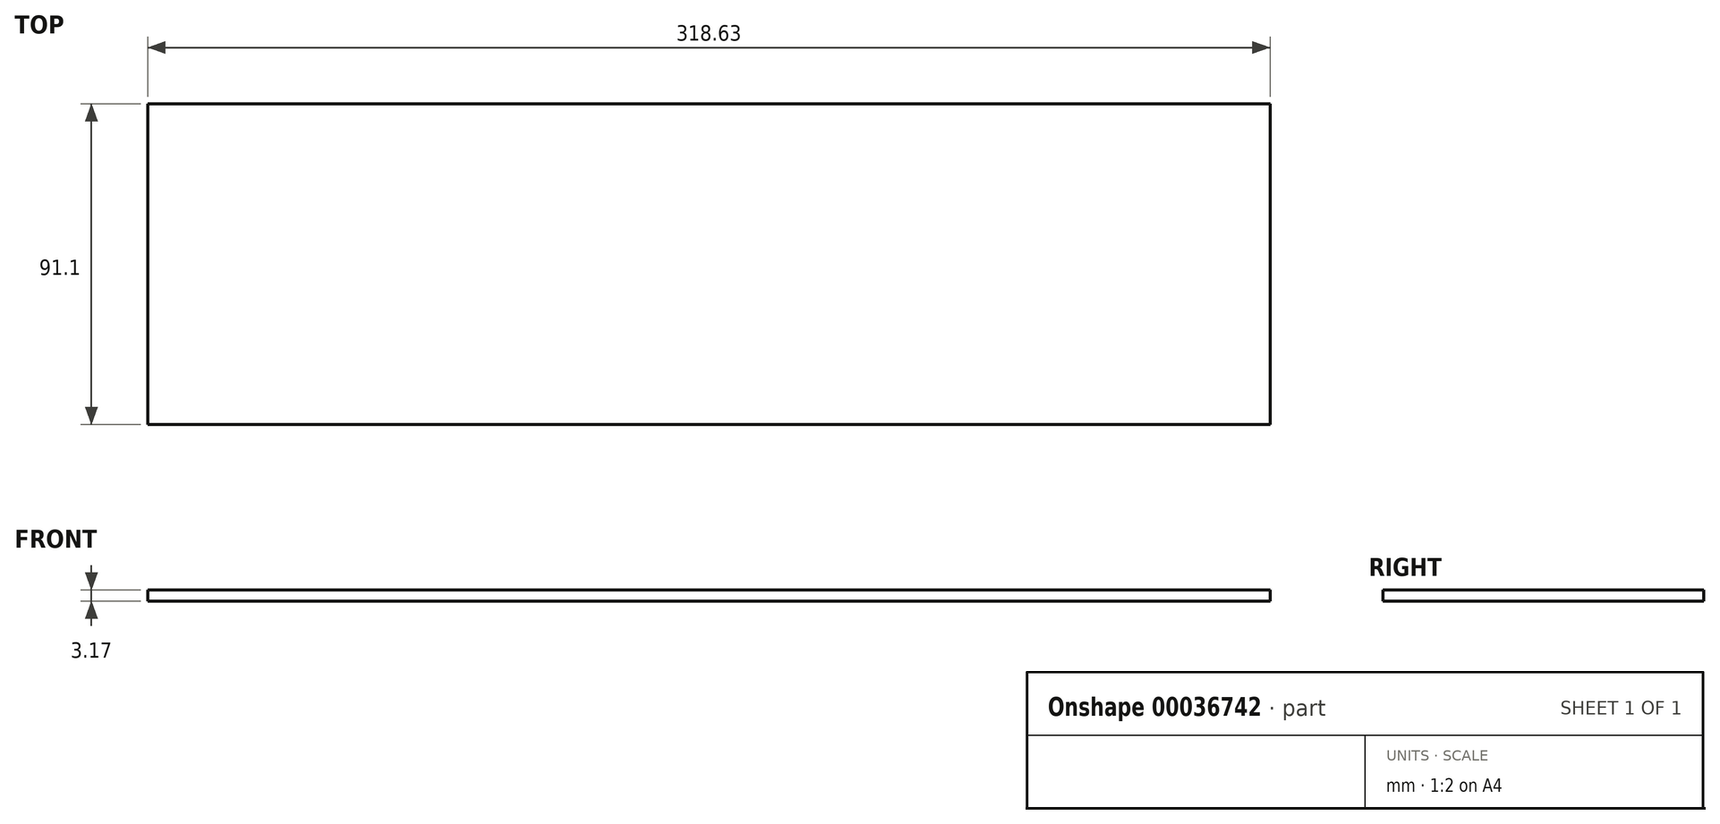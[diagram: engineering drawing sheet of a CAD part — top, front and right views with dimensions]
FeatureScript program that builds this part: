
annotation { "Feature Type Name" : "Feature", "Feature Type Description" : "" }
export const myFeature = defineFeature(function(context is Context, id is Id, definition is map)
    precondition{}
    {
        {
            var Q0;
            Q0=qCreatedBy(makeId("Top.planeOp"),FACE);
            var sketch = newSketch(context, id + "F0", { "sketchPlane" : qUnion([Q0])});
            skLineSegment(sketch, "E0.bottom", {"start": v(-156.5, 2.77) * mm, "end": v(162.12, 2.77) * mm});
            skLineSegment(sketch, "E0.top", {"start": v(-156.5, 93.87) * mm, "end": v(162.12, 93.87) * mm});
            skLineSegment(sketch, "E0.left", {"start": v(-156.5, 2.77) * mm, "end": v(-156.5, 93.87) * mm});
            skLineSegment(sketch, "E0.right", {"start": v(162.12, 2.77) * mm, "end": v(162.12, 93.87) * mm});
            skSolve(sketch);
        }
        {
            var Q0;
            Q0=makeQuery(id+"F0.imprint","IMPRINT",FACE,{"disambiguationData":[TD([[makeQuery(id+"F0.imprint","IMPRINT",EDGE,{"derivedFrom":sQuery(id+"F0.wireOp",EDGE,"E0.bottom")}),1.0]])]});
            extrude(context, id + "F1", {"entities" : qUnion([Q0]), "depth" : 3.17 * mm});
        }
    });
